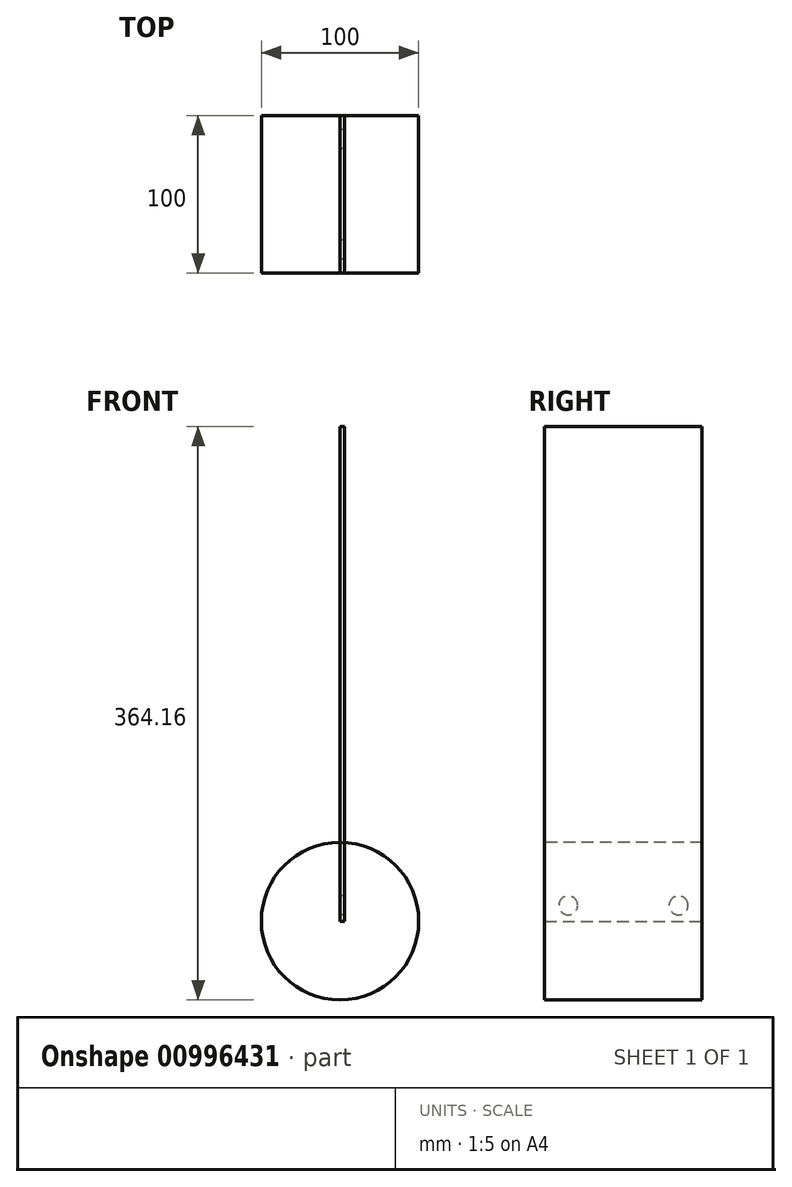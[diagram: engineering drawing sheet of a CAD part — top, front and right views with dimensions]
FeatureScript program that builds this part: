
annotation { "Feature Type Name" : "Feature", "Feature Type Description" : "" }
export const myFeature = defineFeature(function(context is Context, id is Id, definition is map)
    precondition{}
    {
        {
            var Q0;
            Q0=qCreatedBy(makeId("Front.planeOp"),FACE);
            var sketch = newSketch(context, id + "F0", { "sketchPlane" : qUnion([Q0])});
            skCircle(sketch, "E0", {"center": v(0, 0) * mm, "radius": 50 * mm});
            skSolve(sketch);
        }
        {
            var Q0;
            Q0=qCreatedBy(makeId("Right.planeOp"),FACE);
            var sketch = newSketch(context, id + "F1", { "sketchPlane" : qUnion([Q0])});
            skLineSegment(sketch, "E1.bottom", {"start": v(0, 0) * mm, "end": v(100, 0) * mm});
            skLineSegment(sketch, "E1.top", {"start": v(0, 314.16) * mm, "end": v(100, 314.16) * mm});
            skLineSegment(sketch, "E1.left", {"start": v(0, 0) * mm, "end": v(0, 314.16) * mm});
            skLineSegment(sketch, "E1.right", {"start": v(100, 0) * mm, "end": v(100, 314.16) * mm});
            skPoint(sketch, "E2.endSnap0", {"position": v(50, 314.16) * mm});
            skLineSegment(sketch, "E3", {"start": v(85, 10) * mm, "end": v(60, 304.16) * mm, "construction": true});
            skLineSegment(sketch, "E4", {"start": v(60, 304.16) * mm, "end": v(40, 304.16) * mm, "construction": true});
            skLineSegment(sketch, "E5", {"start": v(40, 304.16) * mm, "end": v(15, 10) * mm, "construction": true});
            skPoint(sketch, "E6", {"position": v(15, 10) * mm});
            skPoint(sketch, "E7", {"position": v(85, 10) * mm});
            skPoint(sketch, "E8", {"position": v(40, 304.16) * mm});
            skPoint(sketch, "E9", {"position": v(60, 304.16) * mm});
            skSolve(sketch);
        }
        {
            var Q0;
            Q0=makeQuery(id+"F0.imprint","IMPRINT",FACE,{"disambiguationData":[TD([[makeQuery(id+"F0.imprint","IMPRINT",EDGE,{"derivedFrom":sQuery(id+"F0.wireOp",EDGE,"E0")}),1.0]])]});
            var Q1;
            Q1=sQuery(id+"F0.wireOp",EDGE,"E0");
            extrude(context, id + "F2", {"entities" : qUnion([Q0]), "surfaceEntities" : qUnion([Q1]), "oppositeDirection" : true, "depth" : 100 * mm, "offsetDistance" : 25 * mm});
        }
        {
            var Q0;
            Q0=makeQuery(id+"F1.imprint","IMPRINT",FACE,{"disambiguationData":[TD([[makeQuery(id+"F1.imprint","IMPRINT",EDGE,{"derivedFrom":sQuery(id+"F1.wireOp",EDGE,"E1.bottom")}),1.0]])]});
            extrude(context, id + "F3", {"entities" : qUnion([Q0]), "depth" : 3 * mm, "offsetDistance" : 25 * mm});
        }
        {
            var Q0;
            Q0=qSketchRegion(id+"F1",true);
            var sketch = newSketch(context, id + "F4", { "sketchPlane" : qUnion([Q0])});
            skCircle(sketch, "E10", {"center": v(85, 10) * mm, "radius": 6 * mm});
            skCircle(sketch, "E11", {"center": v(15, 10) * mm, "radius": 6 * mm});
            skSolve(sketch);
        }
        {
            var Q0;
            Q0=makeQuery(id+"F4.imprint","IMPRINT",FACE,{"disambiguationData":[TD([[makeQuery(id+"F4.imprint","IMPRINT",EDGE,{"derivedFrom":sQuery(id+"F4.wireOp",EDGE,"E10")}),1.0]])]});
            var Q1;
            Q1=makeQuery(id+"F4.imprint","IMPRINT",FACE,{"disambiguationData":[TD([[makeQuery(id+"F4.imprint","IMPRINT",EDGE,{"derivedFrom":sQuery(id+"F4.wireOp",EDGE,"E11")}),1.0]])]});
            extrude(context, id + "F5", {"entities" : qUnion([Q0, Q1]), "depth" : 3 * mm, "offsetDistance" : 25 * mm});
        }
    });
